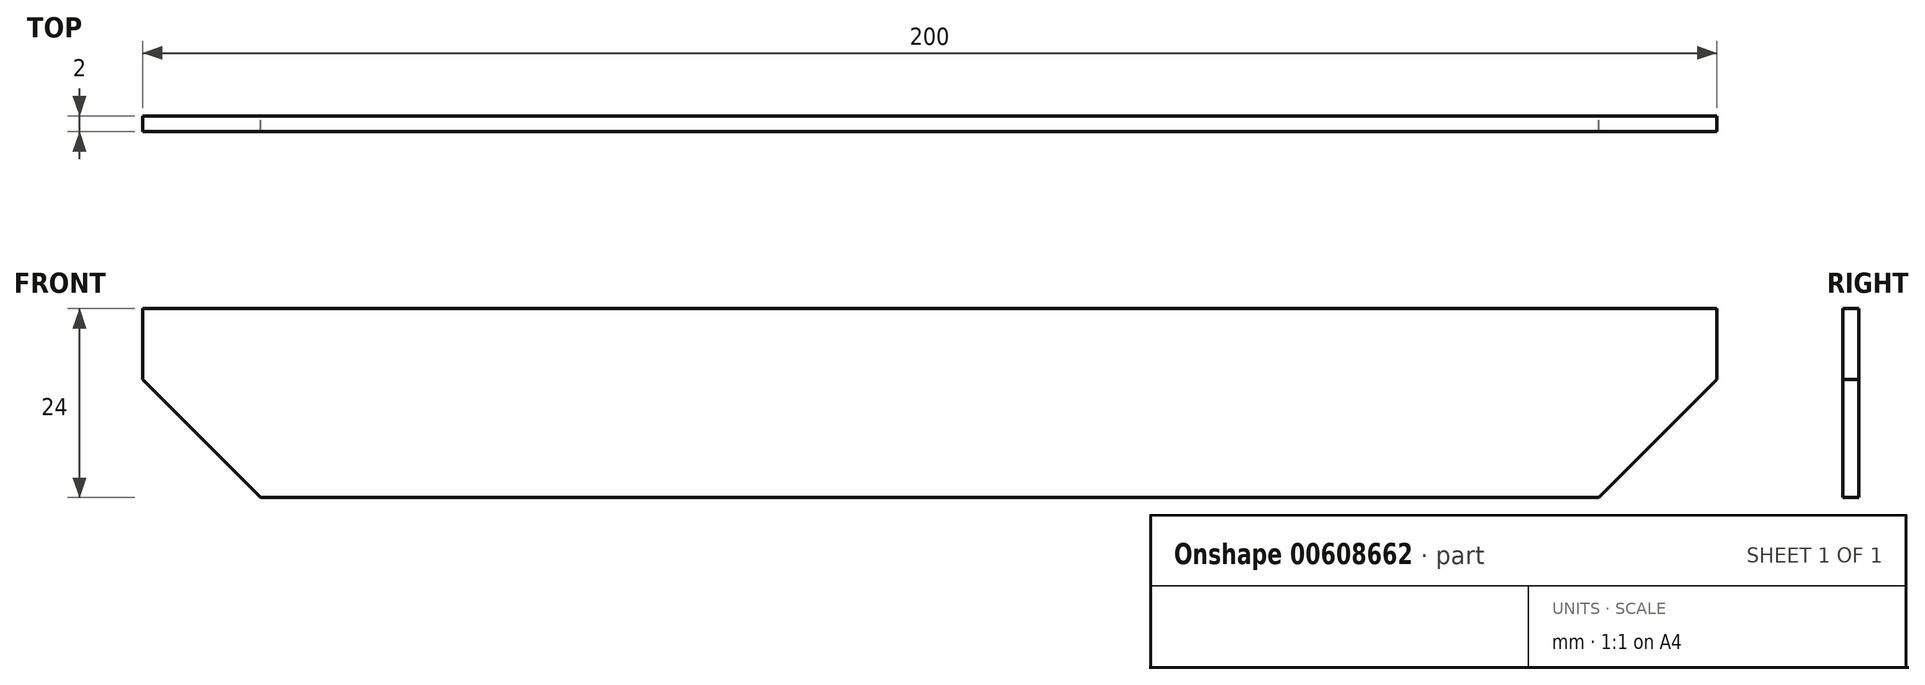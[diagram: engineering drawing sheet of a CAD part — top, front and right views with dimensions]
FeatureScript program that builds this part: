
annotation { "Feature Type Name" : "Feature", "Feature Type Description" : "" }
export const myFeature = defineFeature(function(context is Context, id is Id, definition is map)
    precondition{}
    {
        {
            var Q0;
            Q0=qCreatedBy(makeId("Front.planeOp"),FACE);
            var sketch = newSketch(context, id + "F0", { "sketchPlane" : qUnion([Q0])});
            skLineSegment(sketch, "E0.bottom", {"start": v(85, -7.5) * mm, "end": v(-85, -7.5) * mm});
            skLineSegment(sketch, "E0.top", {"start": v(85, 7.5) * mm, "end": v(-85, 7.5) * mm});
            skLineSegment(sketch, "E0.left", {"start": v(85, -7.5) * mm, "end": v(85, 7.5) * mm});
            skLineSegment(sketch, "E0.right", {"start": v(-85, -7.5) * mm, "end": v(-85, 7.5) * mm});
            skPoint(sketch, "E0.middle", {"position": v(0, 0) * mm});
            skLineSegment(sketch, "E1.bottom", {"start": v(-85, -7.5) * mm, "end": v(-100, -7.5) * mm});
            skLineSegment(sketch, "E1.top", {"start": v(-85, 7.5) * mm, "end": v(-100, 7.5) * mm});
            skLineSegment(sketch, "E1.right", {"start": v(-100, -7.5) * mm, "end": v(-100, 7.5) * mm});
            skPoint(sketch, "E1.middle", {"position": v(-92.5, 0) * mm});
            skLineSegment(sketch, "E2", {"start": v(-100, 7.5) * mm, "end": v(-85, -7.5) * mm});
            skLineSegment(sketch, "E3.bottom", {"start": v(100, -7.5) * mm, "end": v(85, -7.5) * mm});
            skLineSegment(sketch, "E3.top", {"start": v(100, 7.5) * mm, "end": v(85, 7.5) * mm});
            skLineSegment(sketch, "E3.left", {"start": v(100, -7.5) * mm, "end": v(100, 7.5) * mm});
            skPoint(sketch, "E3.middle", {"position": v(92.5, 0) * mm});
            skLineSegment(sketch, "E4", {"start": v(85, -7.5) * mm, "end": v(100, 7.5) * mm});
            skLineSegment(sketch, "E5.bottom", {"start": v(100, 7.5) * mm, "end": v(-100, 7.5) * mm});
            skLineSegment(sketch, "E5.top", {"start": v(100, 16.5) * mm, "end": v(-100, 16.5) * mm});
            skLineSegment(sketch, "E5.left", {"start": v(100, 7.5) * mm, "end": v(100, 16.5) * mm});
            skLineSegment(sketch, "E5.right", {"start": v(-100, 7.5) * mm, "end": v(-100, 16.5) * mm});
            skPoint(sketch, "E5.middle", {"position": v(0, 12) * mm});
            skSolve(sketch);
        }
        {
            var Q0;
            Q0=makeQuery(id+"F0.imprint","IMPRINT",FACE,{"disambiguationData":[TD([[makeQuery(id+"F0.imprint","IMPRINT",EDGE,{"derivedFrom":sQuery(id+"F0.wireOp",EDGE,"E0.bottom")}),-1.0]])]});
            var Q1;
            Q1=makeQuery(id+"F0.imprint","IMPRINT",FACE,{"disambiguationData":[TD([[makeQuery(id+"F0.imprint","IMPRINT",EDGE,{"derivedFrom":sQuery(id+"F0.wireOp",EDGE,"E1.top")}),1.0]])]});
            var Q2;
            Q2=makeQuery(id+"F0.imprint","IMPRINT",FACE,{"disambiguationData":[TD([[makeQuery(id+"F0.imprint","IMPRINT",EDGE,{"derivedFrom":sQuery(id+"F0.wireOp",EDGE,"E3.top")}),1.0]])]});
            var Q3;
            Q3=makeQuery(id+"F0.imprint","IMPRINT",FACE,{"disambiguationData":[TD([[makeQuery(id+"F0.imprint","IMPRINT",EDGE,{"derivedFrom":sQuery(id+"F0.wireOp",EDGE,"OD9o5IjV-5K3p-bvsU-E8e2-8qKfq0g9wVGw.bottom")}),-1.0]])]});
            var Q4;
            {var subQ0=sQuery(id+"F0.wireOp",EDGE,"E0.right");Q4=makeQuery(id+"F0.imprint","IMPRINT",FACE,{"disambiguationData":[TD([[makeQuery(id+"F0.imprint","IMPRINT",EDGE,{"derivedFrom":subQ0}),1.0]])]});}
            var Q5;
            Q5=makeQuery(id+"F0.imprint","IMPRINT",FACE,{"disambiguationData":[TD([[makeQuery(id+"F0.imprint","IMPRINT",EDGE,{"derivedFrom":sQuery(id+"F0.wireOp",EDGE,"E5.top")}),1.0]])]});
            var Q6;
            {var subQ0=sQuery(id+"F0.wireOp",EDGE,"E0.left");Q6=makeQuery(id+"F0.imprint","IMPRINT",FACE,{"disambiguationData":[TD([[makeQuery(id+"F0.imprint","IMPRINT",EDGE,{"derivedFrom":subQ0}),-1.0]])]});}
            extrude(context, id + "F1", {"entities" : qUnion([Q0, Q1, Q2, Q3, Q4, Q5, Q6]), "depth" : 2 * mm, "offsetDistance" : 25 * mm});
        }
    });
